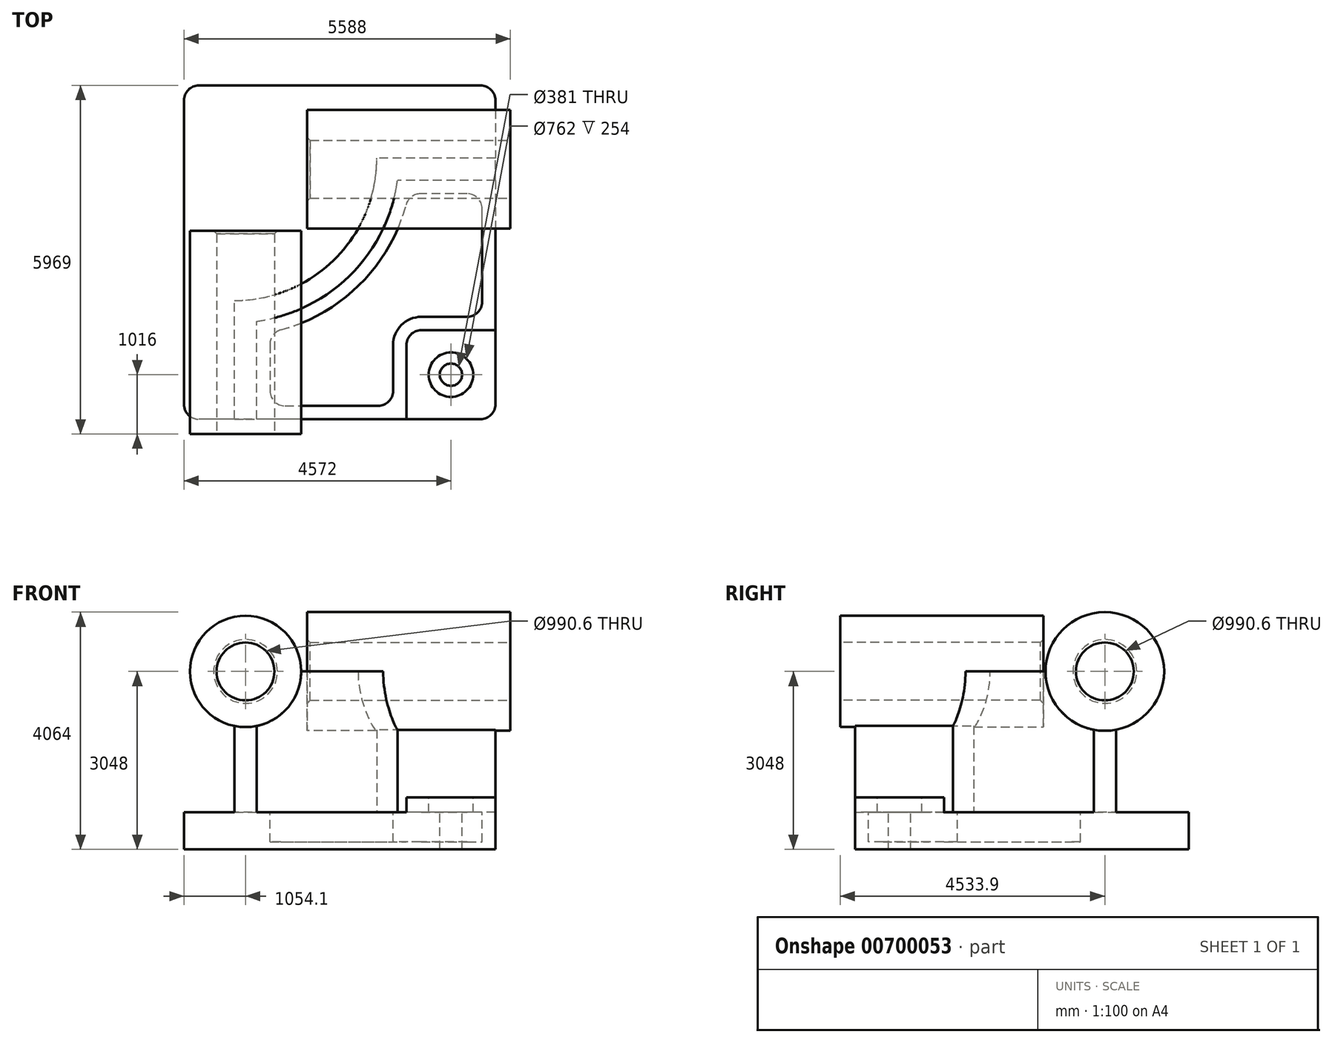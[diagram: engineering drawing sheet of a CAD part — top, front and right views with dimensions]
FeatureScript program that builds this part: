
annotation { "Feature Type Name" : "Feature", "Feature Type Description" : "" }
export const myFeature = defineFeature(function(context is Context, id is Id, definition is map)
    precondition{}
    {
        {
            var Q0;
            Q0=qCreatedBy(makeId("Top.planeOp"),FACE);
            var sketch = newSketch(context, id + "F0", { "sketchPlane" : qUnion([Q0])});
            skLineSegment(sketch, "E0.bottom", {"start": v(3049.56, 2857.5) * mm, "end": v(-2284.44, 2857.5) * mm});
            skLineSegment(sketch, "E0.top", {"start": v(3049.56, -2857.5) * mm, "end": v(-2284.44, -2857.5) * mm});
            skLineSegment(sketch, "E0.left", {"start": v(3049.56, 2857.5) * mm, "end": v(3049.56, -2857.5) * mm});
            skLineSegment(sketch, "E0.right", {"start": v(-2284.44, 2857.5) * mm, "end": v(-2284.44, -2857.5) * mm});
            skPoint(sketch, "E0.middle", {"position": v(382.56, 0) * mm});
            skSolve(sketch);
        }
        {
            var Q0;
            Q0=makeQuery(id+"F0.imprint","IMPRINT",FACE,{"disambiguationData":[TD([[makeQuery(id+"F0.imprint","IMPRINT",EDGE,{"derivedFrom":sQuery(id+"F0.wireOp",EDGE,"E0.bottom")}),1.0]])]});
            extrude(context, id + "F1", {"entities" : qUnion([Q0]), "depth" : 635 * mm, "offsetDistance" : 25.4 * mm});
        }
        {
            var Q0;
            Q0=makeQuery(id+"F1.opExtrude","CAP_FACE",FACE,{"disambiguationData":[OSD([sQuery(id+"F0.wireOp",EDGE,"E0.bottom"),sQuery(id+"F0.wireOp",EDGE,"E0.top"),sQuery(id+"F0.wireOp",EDGE,"E0.left"),sQuery(id+"F0.wireOp",EDGE,"E0.right")])],"isStart":false});
            var sketch = newSketch(context, id + "F2", { "sketchPlane" : qUnion([Q0])});
            skLineSegment(sketch, "E1", {"start": v(-1420.84, -2857.5) * mm, "end": v(-1420.84, -825.5) * mm});
            skLineSegment(sketch, "E2", {"start": v(3049.56, 1612.9) * mm, "end": v(1017.56, 1612.9) * mm});
            skArc(sketch, "E3", {"start": v(-1420.84, -825.5) * mm, "mid": v(303.37, -111.3) * mm, "end": v(1017.56, 1612.9) * mm});
            skLineSegment(sketch, "E4", {"start": v(-1420.84, 1612.9) * mm, "end": v(1017.56, 1612.9) * mm, "construction": true});
            skLineSegment(sketch, "E5", {"start": v(-1420.84, 1612.9) * mm, "end": v(-1420.84, -825.5) * mm, "construction": true});
            skLineSegment(sketch, "E6.0", {"start": v(-1039.84, -2857.5) * mm, "end": v(-1039.84, -1180.64) * mm});
            skArc(sketch, "E6.1", {"start": v(-1039.84, -1180.64) * mm, "mid": v(572.78, -380.72) * mm, "end": v(1372.7, 1231.9) * mm});
            skLineSegment(sketch, "E6.2", {"start": v(3049.56, 1231.9) * mm, "end": v(1372.7, 1231.9) * mm});
            skLineSegment(sketch, "E7.0", {"start": v(3049.56, 2857.5) * mm, "end": v(3049.56, -2857.5) * mm});
            skLineSegment(sketch, "E8.0", {"start": v(3049.56, -2857.5) * mm, "end": v(-2284.44, -2857.5) * mm});
            skLineSegment(sketch, "E9.0.0", {"start": v(-2284.44, -2857.5) * mm, "end": v(3049.56, -2857.5) * mm});
            skLineSegment(sketch, "E9.0.1", {"start": v(3049.56, -2857.5) * mm, "end": v(3049.56, 2857.5) * mm});
            skLineSegment(sketch, "E9.0.2", {"start": v(3049.56, 2857.5) * mm, "end": v(-2284.44, 2857.5) * mm});
            skLineSegment(sketch, "E9.0.3", {"start": v(-2284.44, 2857.5) * mm, "end": v(-2284.44, -2857.5) * mm});
            skSolve(sketch);
        }
        {
            var Q0;
            {var subQ2=sQuery(id+"F2.wireOp",EDGE,"E1");Q0=makeQuery(id+"F2.imprint","IMPRINT",FACE,{"disambiguationData":[TD([[makeQuery(id+"F2.imprint","IMPRINT",EDGE,{"derivedFrom":subQ2}),-1.0]])]});}
            extrude(context, id + "F3", {"entities" : qUnion([Q0]), "operationType" : NewBodyOperationType.ADD, "depth" : 2413 * mm, "offsetDistance" : 25.4 * mm});
        }
        {
            var Q0;
            Q0=makeQuery(id+"F3.boolean.opBoolean","MERGE",FACE,{"derivedFrom":[makeQuery(id+"F1.opExtrude","SWEPT_FACE",FACE,{"disambiguationData":[OSD([sQuery(id+"F0.wireOp",EDGE,"E0.top")])]}),makeQuery(id+"F3.opExtrude","SWEPT_FACE",FACE,{"disambiguationData":[OSD([sQuery(id+"F2.wireOp",EDGE,"E9.0.0")])]})]});
            var sketch = newSketch(context, id + "F4", { "sketchPlane" : qUnion([Q0])});
            skCircle(sketch, "E10", {"center": v(-1230.34, 3048) * mm, "radius": 952.5 * mm});
            skSolve(sketch);
        }
        {
            var Q0;
            Q0 = qSketchRegion(id + "F4", true);
            extrude(context, id + "F5", {"entities" : qUnion([Q0]), "operationType" : NewBodyOperationType.ADD, "depth" : 254 * mm, "offsetDistance" : 25.4 * mm, "hasSecondDirection" : true, "secondDirectionOppositeDirection" : true, "secondDirectionDepth" : 3225.8 * mm});
        }
        {
            var Q0;
            Q0=makeQuery(id+"F3.boolean.opBoolean","MERGE",FACE,{"derivedFrom":[makeQuery(id+"F1.opExtrude","SWEPT_FACE",FACE,{"disambiguationData":[OSD([sQuery(id+"F0.wireOp",EDGE,"E0.left")])]}),makeQuery(id+"F3.opExtrude","SWEPT_FACE",FACE,{"disambiguationData":[OSD([sQuery(id+"F2.wireOp",EDGE,"E9.0.1")])]})]});
            var sketch = newSketch(context, id + "F6", { "sketchPlane" : qUnion([Q0])});
            skCircle(sketch, "E11", {"center": v(1422.4, 3048) * mm, "radius": 1016 * mm});
            skSolve(sketch);
        }
        {
            var Q0;
            Q0 = qSketchRegion(id + "F6", true);
            extrude(context, id + "F7", {"entities" : qUnion([Q0]), "operationType" : NewBodyOperationType.ADD, "depth" : 254 * mm, "offsetDistance" : 25.4 * mm, "hasSecondDirection" : true, "secondDirectionOppositeDirection" : true, "secondDirectionDepth" : 3225.8 * mm});
        }
        {
            var Q0;
            {var subQ0=sQuery(id+"F0.wireOp",EDGE,"E0.left");var subQ1=sQuery(id+"F0.wireOp",EDGE,"E0.top");Q0=makeQuery(id+"F3.boolean.opBoolean","SPLIT",FACE,{"disambiguationData":[TD([makeQuery(id+"F3.opExtrude","SWEPT_FACE",FACE,{"disambiguationData":[OSD([sQuery(id+"F2.wireOp",EDGE,"E6.0")])]})])],"derivedFrom":makeQuery(id+"F1.opExtrude","CAP_FACE",FACE,{"disambiguationData":[OSD([sQuery(id+"F0.wireOp",EDGE,"E0.bottom"),subQ1,subQ0,sQuery(id+"F0.wireOp",EDGE,"E0.right")])],"isStart":false})});}
            var sketch = newSketch(context, id + "F8", { "sketchPlane" : qUnion([Q0])});
            skLineSegment(sketch, "E12.bottom", {"start": v(3049.56, -2857.5) * mm, "end": v(1525.56, -2857.5) * mm});
            skLineSegment(sketch, "E12.top", {"start": v(3049.56, -1333.5) * mm, "end": v(1525.56, -1333.5) * mm});
            skLineSegment(sketch, "E12.left", {"start": v(3049.56, -2857.5) * mm, "end": v(3049.56, -1333.5) * mm});
            skLineSegment(sketch, "E12.right", {"start": v(1525.56, -2857.5) * mm, "end": v(1525.56, -1333.5) * mm});
            skSolve(sketch);
        }
        {
            var Q0;
            Q0 = qSketchRegion(id + "F8", true);
            extrude(context, id + "F9", {"entities" : qUnion([Q0]), "operationType" : NewBodyOperationType.ADD, "depth" : 254 * mm, "offsetDistance" : 25.4 * mm});
        }
        {
            var Q0;
            Q0=makeQuery(id+"F9.opExtrude","SWEPT_EDGE",EDGE,{"disambiguationData":[OSD([sQuery(id+"F8.wireOp",EDGE,"E12.top"),sQuery(id+"F8.wireOp",EDGE,"E12.right")])]});
            fillet(context, id + "F10", {"entities" : qUnion([Q0]), "radius" : 254 * mm, "tangentPropagation" : true, "allowEdgeOverflow" : false});
        }
        {
            var Q0;
            {var subQ0=sQuery(id+"F0.wireOp",EDGE,"E0.left");var subQ1=sQuery(id+"F0.wireOp",EDGE,"E0.top");Q0=makeQuery(id+"F3.boolean.opBoolean","SPLIT",FACE,{"disambiguationData":[TD([makeQuery(id+"F3.opExtrude","SWEPT_FACE",FACE,{"disambiguationData":[OSD([sQuery(id+"F2.wireOp",EDGE,"E6.0")])]})])],"derivedFrom":makeQuery(id+"F1.opExtrude","CAP_FACE",FACE,{"disambiguationData":[OSD([sQuery(id+"F0.wireOp",EDGE,"E0.bottom"),subQ1,subQ0,sQuery(id+"F0.wireOp",EDGE,"E0.right")])],"isStart":false})});}
            var sketch = newSketch(context, id + "F11", { "sketchPlane" : qUnion([Q0])});
            skLineSegment(sketch, "E13.0", {"start": v(-811.24, -1373.52) * mm, "end": v(-811.24, -2628.9) * mm});
            skArc(sketch, "E13.1", {"start": v(1565.58, 1003.3) * mm, "mid": v(734.42, -542.36) * mm, "end": v(-811.24, -1373.52) * mm});
            skLineSegment(sketch, "E13.2", {"start": v(-811.24, -2628.9) * mm, "end": v(1296.96, -2628.9) * mm});
            skLineSegment(sketch, "E13.3", {"start": v(2820.96, 1003.3) * mm, "end": v(1565.58, 1003.3) * mm});
            skLineSegment(sketch, "E13.4", {"start": v(1296.96, -2628.9) * mm, "end": v(1296.96, -1587.5) * mm});
            skArc(sketch, "E13.5", {"start": v(1296.96, -1587.5) * mm, "mid": v(1438.31, -1246.25) * mm, "end": v(1779.56, -1104.9) * mm});
            skLineSegment(sketch, "E13.6", {"start": v(1779.56, -1104.9) * mm, "end": v(2820.96, -1104.9) * mm});
            skLineSegment(sketch, "E13.7", {"start": v(2820.96, -1104.9) * mm, "end": v(2820.96, 1003.3) * mm});
            skSolve(sketch);
        }
        {
            var Q0;
            Q0=makeQuery(id+"F11.imprint","IMPRINT",FACE,{"disambiguationData":[TD([[makeQuery(id+"F11.imprint","IMPRINT",EDGE,{"derivedFrom":sQuery(id+"F11.wireOp",EDGE,"E13.0")}),1.0]])]});
            extrude(context, id + "F12", {"entities" : qUnion([Q0]), "operationType" : NewBodyOperationType.REMOVE, "oppositeDirection" : true, "depth" : 508 * mm, "offsetDistance" : 25.4 * mm});
        }
        {
            var Q0;
            Q0=makeQuery(id+"F9.opExtrude","CAP_FACE",FACE,{"disambiguationData":[OSD([sQuery(id+"F8.wireOp",EDGE,"E12.bottom"),sQuery(id+"F8.wireOp",EDGE,"E12.top"),sQuery(id+"F8.wireOp",EDGE,"E12.left"),sQuery(id+"F8.wireOp",EDGE,"E12.right")])],"isStart":false});
            var sketch = newSketch(context, id + "F13", { "sketchPlane" : qUnion([Q0])});
            skCircle(sketch, "E14", {"center": v(2287.56, -2095.5) * mm, "radius": 381 * mm});
            skSolve(sketch);
        }
        {
            var Q0;
            Q0=sQuery(id+"F13.wireOp",VERTEX,"E14.center");
            var Q1;
            Q1=makeQuery(id+"F1.opExtrude","SWEPT_BODY",BODY,{"disambiguationData":[OSD([sQuery(id+"F0.wireOp",EDGE,"E0.bottom"),sQuery(id+"F0.wireOp",EDGE,"E0.top"),sQuery(id+"F0.wireOp",EDGE,"E0.left"),sQuery(id+"F0.wireOp",EDGE,"E0.right")])]});
            hole(context, id + "F14", {"style" : HoleStyle.C_BORE, "endStyle" : HoleEndStyle.THROUGH, "holeDiameter" : 381 * mm, "cBoreDiameter" : 762 * mm, "cBoreDepth" : 254 * mm, "majorDiameter" : 6.35 * mm, "isTappedThrough" : true, "tappedDepth" : 12.7 * mm, "tapClearance" : 3, "locations" : qUnion([Q0]), "scope" : qUnion([Q1])});
        }
        {
            var Q0;
            Q0=makeQuery(id+"F12.boolean.opBoolean","COPY",EDGE,{"derivedFrom":makeQuery(id+"F12.opExtrude","SWEPT_EDGE",EDGE,{"disambiguationData":[OSD([sQuery(id+"F11.wireOp",EDGE,"E13.0"),sQuery(id+"F11.wireOp",EDGE,"E13.1")])]})});
            var Q1;
            Q1=makeQuery(id+"F12.boolean.opBoolean","COPY",EDGE,{"derivedFrom":makeQuery(id+"F12.opExtrude","SWEPT_EDGE",EDGE,{"disambiguationData":[OSD([sQuery(id+"F11.wireOp",EDGE,"E13.1"),sQuery(id+"F11.wireOp",EDGE,"E13.3")])]})});
            var Q2;
            Q2=makeQuery(id+"F12.boolean.opBoolean","COPY",EDGE,{"derivedFrom":makeQuery(id+"F12.opExtrude","SWEPT_EDGE",EDGE,{"disambiguationData":[OSD([sQuery(id+"F11.wireOp",EDGE,"E13.0"),sQuery(id+"F11.wireOp",EDGE,"E13.2")])]})});
            var Q3;
            Q3=makeQuery(id+"F12.boolean.opBoolean","COPY",EDGE,{"derivedFrom":makeQuery(id+"F12.opExtrude","SWEPT_EDGE",EDGE,{"disambiguationData":[OSD([sQuery(id+"F11.wireOp",EDGE,"E13.3"),sQuery(id+"F11.wireOp",EDGE,"E13.7")])]})});
            var Q4;
            Q4=makeQuery(id+"F12.boolean.opBoolean","COPY",EDGE,{"derivedFrom":makeQuery(id+"F12.opExtrude","SWEPT_EDGE",EDGE,{"disambiguationData":[OSD([sQuery(id+"F11.wireOp",EDGE,"E13.2"),sQuery(id+"F11.wireOp",EDGE,"E13.4")])]})});
            var Q5;
            Q5=makeQuery(id+"F12.boolean.opBoolean","COPY",EDGE,{"derivedFrom":makeQuery(id+"F12.opExtrude","SWEPT_EDGE",EDGE,{"disambiguationData":[OSD([sQuery(id+"F11.wireOp",EDGE,"E13.6"),sQuery(id+"F11.wireOp",EDGE,"E13.7")])]})});
            fillet(context, id + "F15", {"entities" : qUnion([Q0, Q1, Q2, Q3, Q4, Q5]), "radius" : 254 * mm, "tangentPropagation" : true, "allowEdgeOverflow" : false});
        }
        {
            var Q0;
            Q0=makeQuery(id+"F5.opExtrude","CAP_FACE",FACE,{"disambiguationData":[OSD([sQuery(id+"F4.wireOp",EDGE,"E10")])],"isStart":false});
            var sketch = newSketch(context, id + "F16", { "sketchPlane" : qUnion([Q0])});
            skCircle(sketch, "E15", {"center": v(-1230.34, 3048) * mm, "radius": 495.3 * mm});
            skSolve(sketch);
        }
        {
            var Q0;
            Q0 = qSketchRegion(id + "F16", true);
            extrude(context, id + "F17", {"entities" : qUnion([Q0]), "operationType" : NewBodyOperationType.REMOVE, "endBound" : BoundingType.THROUGH_ALL, "oppositeDirection" : true, "depth" : 25.4 * mm, "offsetDistance" : 25.4 * mm});
        }
        {
            var Q0;
            Q0=makeQuery(id+"F7.opExtrude","CAP_FACE",FACE,{"disambiguationData":[OSD([sQuery(id+"F6.wireOp",EDGE,"E11")])],"isStart":false});
            var sketch = newSketch(context, id + "F18", { "sketchPlane" : qUnion([Q0])});
            skCircle(sketch, "E16", {"center": v(1422.4, 3048) * mm, "radius": 495.3 * mm});
            skSolve(sketch);
        }
        {
            var Q0;
            Q0 = qSketchRegion(id + "F18", true);
            extrude(context, id + "F19", {"entities" : qUnion([Q0]), "operationType" : NewBodyOperationType.REMOVE, "endBound" : BoundingType.THROUGH_ALL, "oppositeDirection" : true, "depth" : 25.4 * mm, "offsetDistance" : 25.4 * mm});
        }
        {
            var Q0;
            Q0=makeQuery(id+"F17.boolean.opBoolean","COPY",EDGE,{"derivedFrom":makeQuery(id+"F17.opExtrude","CAP_EDGE",EDGE,{"disambiguationData":[OSD([sQuery(id+"F16.wireOp",EDGE,"E15")])],"isStart":true})});
            var Q1;
            Q1=makeQuery(id+"F19.boolean.opBoolean","COPY",EDGE,{"derivedFrom":makeQuery(id+"F19.opExtrude","CAP_EDGE",EDGE,{"disambiguationData":[OSD([sQuery(id+"F18.wireOp",EDGE,"E16")])],"isStart":true})});
            var Q2;
            Q2=makeQuery(id+"F17.boolean.opBoolean","INTERSECT",EDGE,{"derivedFrom":[makeQuery(id+"F5.opExtrude","CAP_FACE",FACE,{"disambiguationData":[OSD([sQuery(id+"F4.wireOp",EDGE,"E10")])],"isStart":true}),makeQuery(id+"F17.opExtrude","SWEPT_FACE",FACE,{"disambiguationData":[OSD([sQuery(id+"F16.wireOp",EDGE,"E15")])]})]});
            var Q3;
            Q3=makeQuery(id+"F19.boolean.opBoolean","INTERSECT",EDGE,{"derivedFrom":[makeQuery(id+"F7.opExtrude","CAP_FACE",FACE,{"disambiguationData":[OSD([sQuery(id+"F6.wireOp",EDGE,"E11")])],"isStart":true}),makeQuery(id+"F19.opExtrude","SWEPT_FACE",FACE,{"disambiguationData":[OSD([sQuery(id+"F18.wireOp",EDGE,"E16")])]})]});
            chamfer(context, id + "F20", {"entities" : qUnion([Q0, Q1, Q2, Q3]), "width" : 50.8 * mm, "tangentPropagation" : true});
        }
        {
            var Q0;
            Q0=makeQuery(id+"F1.opExtrude","SWEPT_EDGE",EDGE,{"disambiguationData":[OSD([sQuery(id+"F0.wireOp",EDGE,"E0.top"),sQuery(id+"F0.wireOp",EDGE,"E0.right")])]});
            var Q1;
            Q1=makeQuery(id+"F9.boolean.opBoolean","MERGE",EDGE,{"derivedFrom":[makeQuery(id+"F1.opExtrude","SWEPT_EDGE",EDGE,{"disambiguationData":[OSD([sQuery(id+"F0.wireOp",EDGE,"E0.top"),sQuery(id+"F0.wireOp",EDGE,"E0.left")])]}),makeQuery(id+"F9.opExtrude","SWEPT_EDGE",EDGE,{"disambiguationData":[OSD([sQuery(id+"F8.wireOp",EDGE,"E12.bottom"),sQuery(id+"F8.wireOp",EDGE,"E12.left")])]})]});
            var Q2;
            Q2=makeQuery(id+"F1.opExtrude","SWEPT_EDGE",EDGE,{"disambiguationData":[OSD([sQuery(id+"F0.wireOp",EDGE,"E0.bottom"),sQuery(id+"F0.wireOp",EDGE,"E0.left")])]});
            var Q3;
            Q3=makeQuery(id+"F1.opExtrude","SWEPT_EDGE",EDGE,{"disambiguationData":[OSD([sQuery(id+"F0.wireOp",EDGE,"E0.bottom"),sQuery(id+"F0.wireOp",EDGE,"E0.right")])]});
            fillet(context, id + "F21", {"entities" : qUnion([Q0, Q1, Q2, Q3]), "radius" : 254 * mm, "tangentPropagation" : true, "allowEdgeOverflow" : false});
        }
    });
